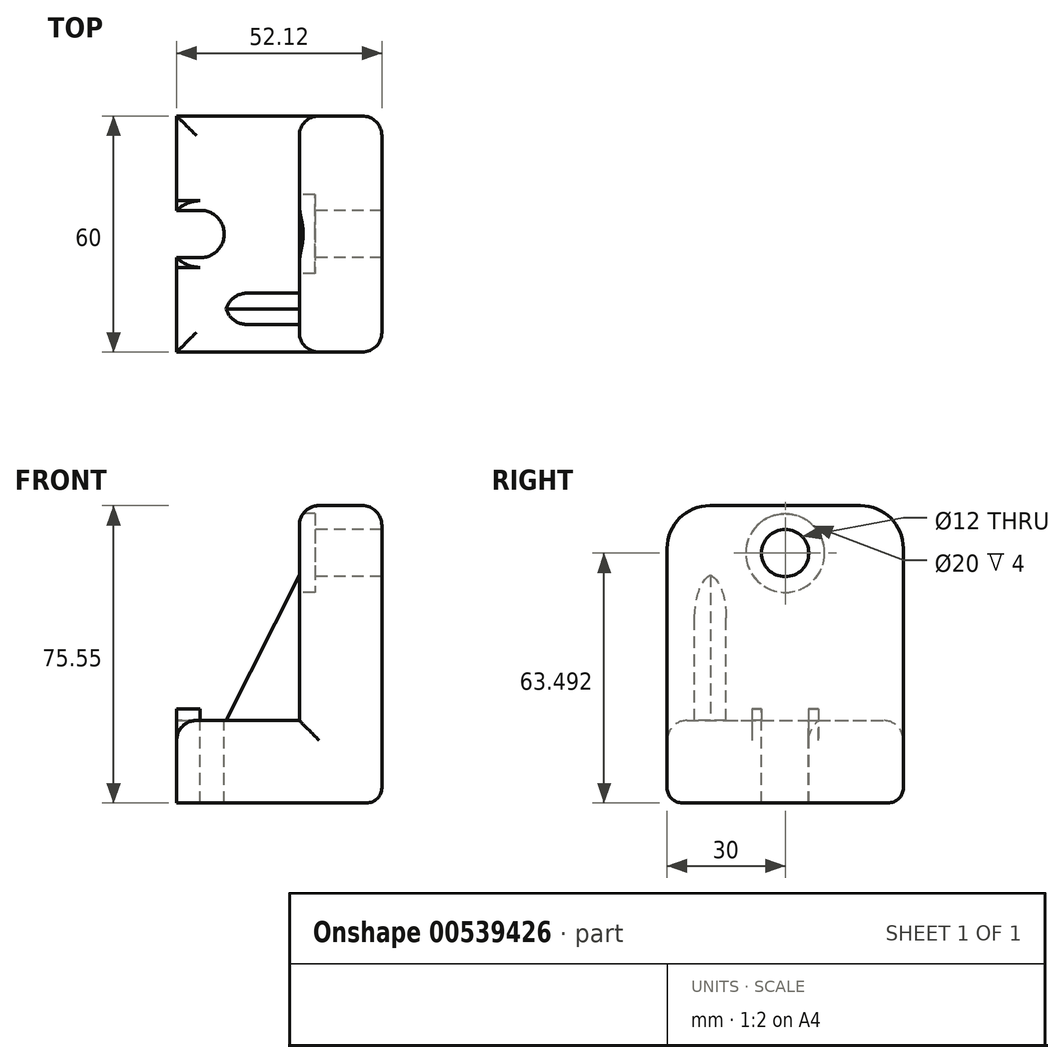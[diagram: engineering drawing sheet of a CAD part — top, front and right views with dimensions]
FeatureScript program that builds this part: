
annotation { "Feature Type Name" : "Feature", "Feature Type Description" : "" }
export const myFeature = defineFeature(function(context is Context, id is Id, definition is map)
    precondition{}
    {
        {
            var Q0;
            Q0=qCreatedBy(makeId("Front.planeOp"),FACE);
            var sketch = newSketch(context, id + "F0", { "sketchPlane" : qUnion([Q0])});
            skLineSegment(sketch, "E0", {"start": v(0, 0) * mm, "end": v(0, 54.6) * mm});
            skLineSegment(sketch, "E1", {"start": v(0, 54.6) * mm, "end": v(20.95, 54.6) * mm});
            skLineSegment(sketch, "E2", {"start": v(20.95, 54.6) * mm, "end": v(20.95, -20.95) * mm});
            skLineSegment(sketch, "E3", {"start": v(20.95, -20.95) * mm, "end": v(-31.17, -20.95) * mm});
            skLineSegment(sketch, "E4", {"start": v(-31.17, -20.95) * mm, "end": v(-31.17, 0) * mm});
            skLineSegment(sketch, "E5", {"start": v(-31.17, 0) * mm, "end": v(0, 0) * mm});
            skSolve(sketch);
        }
        {
            var Q0;
            Q0=makeQuery(id+"F0.imprint","IMPRINT",FACE,{"disambiguationData":[TD([[makeQuery(id+"F0.imprint","IMPRINT",EDGE,{"derivedFrom":sQuery(id+"F0.wireOp",EDGE,"E0")}),-1.0]])]});
            extrude(context, id + "F1", {"entities" : qUnion([Q0]), "endBound" : BoundingType.SYMMETRIC, "depth" : 60 * mm, "offsetDistance" : 25 * mm});
        }
        {
            var Q0;
            Q0=makeQuery(id+"F1.opExtrude","SWEPT_FACE",FACE,{"disambiguationData":[OSD([sQuery(id+"F0.wireOp",EDGE,"E0")])]});
            var sketch = newSketch(context, id + "F2", { "sketchPlane" : qUnion([Q0])});
            skCircle(sketch, "E6", {"center": v(0, 42.54) * mm, "radius": 6 * mm});
            skSolve(sketch);
        }
        {
            var Q0;
            Q0=makeQuery(id+"F2.imprint","IMPRINT",FACE,{"disambiguationData":[TD([[makeQuery(id+"F2.imprint","IMPRINT",EDGE,{"derivedFrom":sQuery(id+"F2.wireOp",EDGE,"E6")}),1.0]])]});
            extrude(context, id + "F3", {"entities" : qUnion([Q0]), "operationType" : NewBodyOperationType.REMOVE, "endBound" : BoundingType.THROUGH_ALL, "oppositeDirection" : true, "depth" : 25 * mm, "offsetDistance" : 25 * mm});
        }
        {
            var Q0;
            Q0=makeQuery(id+"F1.opExtrude","SWEPT_FACE",FACE,{"disambiguationData":[OSD([sQuery(id+"F0.wireOp",EDGE,"E0")])]});
            var sketch = newSketch(context, id + "F4", { "sketchPlane" : qUnion([Q0])});
            skCircle(sketch, "E7", {"center": v(0, 42.54) * mm, "radius": 10 * mm});
            skSolve(sketch);
        }
        {
            var Q0;
            Q0=makeQuery(id+"F4.imprint","IMPRINT",FACE,{"disambiguationData":[TD([[makeQuery(id+"F4.imprint","IMPRINT",EDGE,{"derivedFrom":sQuery(id+"F4.wireOp",EDGE,"E7")}),1.0]])]});
            extrude(context, id + "F5", {"entities" : qUnion([Q0]), "operationType" : NewBodyOperationType.REMOVE, "oppositeDirection" : true, "depth" : 4 * mm, "offsetDistance" : 25 * mm});
        }
        {
            var Q0;
            Q0=makeQuery(id+"F1.opExtrude","SWEPT_FACE",FACE,{"disambiguationData":[OSD([sQuery(id+"F0.wireOp",EDGE,"E5")])]});
            var sketch = newSketch(context, id + "F6", { "sketchPlane" : qUnion([Q0])});
            skCircle(sketch, "E8", {"center": v(-25.09, 0) * mm, "radius": 6 * mm});
            skLineSegment(sketch, "E9", {"start": v(-25.17, 6) * mm, "end": v(-31.17, 5.92) * mm});
            skLineSegment(sketch, "E10", {"start": v(-25.17, -6) * mm, "end": v(-31.17, -6) * mm});
            skSolve(sketch);
        }
        {
            var Q0;
            {var subQ0=sQuery(id+"F6.wireOp",EDGE,"E8");var subQ1=makeQuery(id+"F6.imprint","INTERSECT",VERTEX,{"derivedFrom":[subQ0,sQuery(id+"F6.wireOp",EDGE,"E9")]});Q0=makeQuery(id+"F6.imprint","IMPRINT",FACE,{"disambiguationData":[TD([[makeQuery(id+"F6.imprint","IMPRINT",EDGE,{"disambiguationData":[TD([[subQ1,-1.0]])],"derivedFrom":subQ0}),1.0]])]});}
            var Q1;
            {var subQ0=sQuery(id+"F6.wireOp",EDGE,"E9");Q1=makeQuery(id+"F6.imprint","IMPRINT",FACE,{"disambiguationData":[TD([[makeQuery(id+"F6.imprint","IMPRINT",EDGE,{"derivedFrom":subQ0}),1.0]])]});}
            extrude(context, id + "F7", {"entities" : qUnion([Q0, Q1]), "operationType" : NewBodyOperationType.REMOVE, "endBound" : BoundingType.THROUGH_ALL, "oppositeDirection" : true, "depth" : 25 * mm, "offsetDistance" : 25 * mm});
        }
        {
            var Q0;
            Q0=makeQuery(id+"F1.opExtrude","CAP_EDGE",EDGE,{"disambiguationData":[OSD([sQuery(id+"F0.wireOp",EDGE,"E1")])],"isStart":false});
            var Q1;
            Q1=makeQuery(id+"F1.opExtrude","CAP_EDGE",EDGE,{"disambiguationData":[OSD([sQuery(id+"F0.wireOp",EDGE,"E1")])],"isStart":true});
            fillet(context, id + "F8", {"entities" : qUnion([Q0, Q1]), "radius" : 10.86 * mm, "tangentPropagation" : true, "allowEdgeOverflow" : false});
        }
        {
            var Q0;
            Q0=qCreatedBy(makeId("Front.planeOp"),FACE);
            cPlane(context, id + "F9", {"entities" : qUnion([Q0]), "cplaneType" : CPlaneType.OFFSET, "offset" : 15 * mm, "width" : 150 * mm, "height" : 150 * mm});
        }
        {
            var Q0;
            Q0=qCreatedBy(id+"F9.planeOp",FACE);
            var sketch = newSketch(context, id + "F10", { "sketchPlane" : qUnion([Q0])});
            skLineSegment(sketch, "E11.0", {"start": v(0, 0) * mm, "end": v(0, 37.18) * mm});
            skLineSegment(sketch, "E11.1", {"start": v(-18.67, 0) * mm, "end": v(0, 0) * mm});
            skLineSegment(sketch, "E12", {"start": v(0, 37.18) * mm, "end": v(-18.67, 0) * mm});
            skSolve(sketch);
        }
        {
            var Q0;
            Q0=makeQuery(id+"F10.imprint","IMPRINT",FACE,{"disambiguationData":[TD([[makeQuery(id+"F10.imprint","IMPRINT",EDGE,{"derivedFrom":sQuery(id+"F10.wireOp",EDGE,"E11.0")}),1.0]])]});
            extrude(context, id + "F11", {"entities" : qUnion([Q0]), "operationType" : NewBodyOperationType.ADD, "depth" : 8 * mm, "offsetDistance" : 25 * mm});
        }
        {
            var Q0;
            Q0=makeQuery(id+"F1.opExtrude","SWEPT_FACE",FACE,{"disambiguationData":[OSD([sQuery(id+"F0.wireOp",EDGE,"E5")])]});
            var sketch = newSketch(context, id + "F12", { "sketchPlane" : qUnion([Q0])});
            skCircle(sketch, "E13", {"center": v(-25.17, 0) * mm, "radius": 8.47 * mm});
            skLineSegment(sketch, "E14", {"start": v(-31.17, 8.47) * mm, "end": v(-25.17, 8.47) * mm});
            skLineSegment(sketch, "E15", {"start": v(-25.17, -8.47) * mm, "end": v(-31.17, -8.47) * mm});
            skSolve(sketch);
        }
        {
            var Q0;
            {var subQ0=makeQuery(id+"F7.boolean.opBoolean","COPY",EDGE,{"derivedFrom":makeQuery(id+"F7.opExtrude","CAP_EDGE",EDGE,{"disambiguationData":[OSD([sQuery(id+"F6.wireOp",EDGE,"E8")])],"isStart":true})});Q0=makeQuery(id+"F12.imprint","IMPRINT",FACE,{"disambiguationData":[TD([[makeQuery(id+"F12.imprint","IMPRINT",EDGE,{"derivedFrom":subQ0}),-1.0]])]});}
            var Q1;
            {var subQ0=sQuery(id+"F12.wireOp",EDGE,"E15");Q1=makeQuery(id+"F12.imprint","IMPRINT",FACE,{"disambiguationData":[TD([[makeQuery(id+"F12.imprint","IMPRINT",EDGE,{"derivedFrom":subQ0}),-1.0]])]});}
            var Q2;
            {var subQ0=sQuery(id+"F12.wireOp",EDGE,"E14");Q2=makeQuery(id+"F12.imprint","IMPRINT",FACE,{"disambiguationData":[TD([[makeQuery(id+"F12.imprint","IMPRINT",EDGE,{"derivedFrom":subQ0}),-1.0]])]});}
            extrude(context, id + "F13", {"entities" : qUnion([Q0, Q1, Q2]), "operationType" : NewBodyOperationType.ADD, "depth" : 3 * mm, "offsetDistance" : 25 * mm});
        }
        {
            var Q0;
            Q0=makeQuery(id+"F1.opExtrude","CAP_EDGE",EDGE,{"disambiguationData":[OSD([sQuery(id+"F0.wireOp",EDGE,"E0")])],"isStart":false});
            var Q1;
            Q1=makeQuery(id+"F1.opExtrude","CAP_EDGE",EDGE,{"disambiguationData":[OSD([sQuery(id+"F0.wireOp",EDGE,"E5")])],"isStart":false});
            var Q2;
            {var subQ0=sQuery(id+"F0.wireOp",EDGE,"E5");var subQ1=sQuery(id+"F0.wireOp",EDGE,"E4");Q2=makeQuery(id+"F7.boolean.opBoolean","SPLIT",EDGE,{"disambiguationData":[TD([makeQuery(id+"F7.opExtrude","SWEPT_FACE",FACE,{"disambiguationData":[OSD([sQuery(id+"F6.wireOp",EDGE,"E10")])]})])],"derivedFrom":makeQuery(id+"F1.opExtrude","SWEPT_EDGE",EDGE,{"disambiguationData":[OSD([subQ1,subQ0])]})});}
            var Q3;
            {var subQ0=sQuery(id+"F0.wireOp",EDGE,"E5");var subQ1=sQuery(id+"F0.wireOp",EDGE,"E4");Q3=makeQuery(id+"F7.boolean.opBoolean","SPLIT",EDGE,{"disambiguationData":[TD([makeQuery(id+"F7.opExtrude","SWEPT_FACE",FACE,{"disambiguationData":[OSD([sQuery(id+"F6.wireOp",EDGE,"E9")])]})])],"derivedFrom":makeQuery(id+"F1.opExtrude","SWEPT_EDGE",EDGE,{"disambiguationData":[OSD([subQ1,subQ0])]})});}
            var Q4;
            Q4=makeQuery(id+"F1.opExtrude","CAP_EDGE",EDGE,{"disambiguationData":[OSD([sQuery(id+"F0.wireOp",EDGE,"E5")])],"isStart":true});
            var Q5;
            Q5=makeQuery(id+"F1.opExtrude","CAP_EDGE",EDGE,{"disambiguationData":[OSD([sQuery(id+"F0.wireOp",EDGE,"E2")])],"isStart":true});
            var Q6;
            Q6=makeQuery(id+"F11.opExtrude","CAP_EDGE",EDGE,{"disambiguationData":[OSD([sQuery(id+"F10.wireOp",EDGE,"E12")])],"isStart":true});
            var Q7;
            Q7=makeQuery(id+"F11.opExtrude","CAP_EDGE",EDGE,{"disambiguationData":[OSD([sQuery(id+"F10.wireOp",EDGE,"E12")])],"isStart":false});
            var Q8;
            Q8=makeQuery(id+"FK36l31Y0CoLxMm_1.1.F11.opExtrude","CAP_EDGE",EDGE,{"disambiguationData":[OSD([sQuery(id+"F10.wireOp",EDGE,"E12")])],"isStart":true});
            var Q9;
            Q9=makeQuery(id+"FK36l31Y0CoLxMm_1.1.F11.opExtrude","CAP_EDGE",EDGE,{"disambiguationData":[OSD([sQuery(id+"F10.wireOp",EDGE,"E12")])],"isStart":false});
            fillet(context, id + "F14", {"entities" : qUnion([Q0, Q1, Q2, Q3, Q4, Q5, Q6, Q7, Q8, Q9]), "radius" : 5 * mm, "tangentPropagation" : true, "allowEdgeOverflow" : false});
        }
        {
            var Q0;
            Q0=makeQuery(id+"F14.opFillet","BLEND_EDGE",EDGE,{"blendedFrom":[makeQuery(id+"F1.opExtrude","CAP_EDGE",EDGE,{"disambiguationData":[OSD([sQuery(id+"F0.wireOp",EDGE,"E2")])],"isStart":false}),makeQuery(id+"F1.opExtrude","SWEPT_FACE",FACE,{"disambiguationData":[OSD([sQuery(id+"F0.wireOp",EDGE,"E3")])]})],"blendedInto":[makeQuery(id+"F1.opExtrude","SWEPT_FACE",FACE,{"disambiguationData":[OSD([sQuery(id+"F0.wireOp",EDGE,"E3")])]})]});
            fillet(context, id + "F15", {"entities" : qUnion([Q0]), "radius" : 3.86 * mm, "tangentPropagation" : true, "allowEdgeOverflow" : false});
        }
    });
